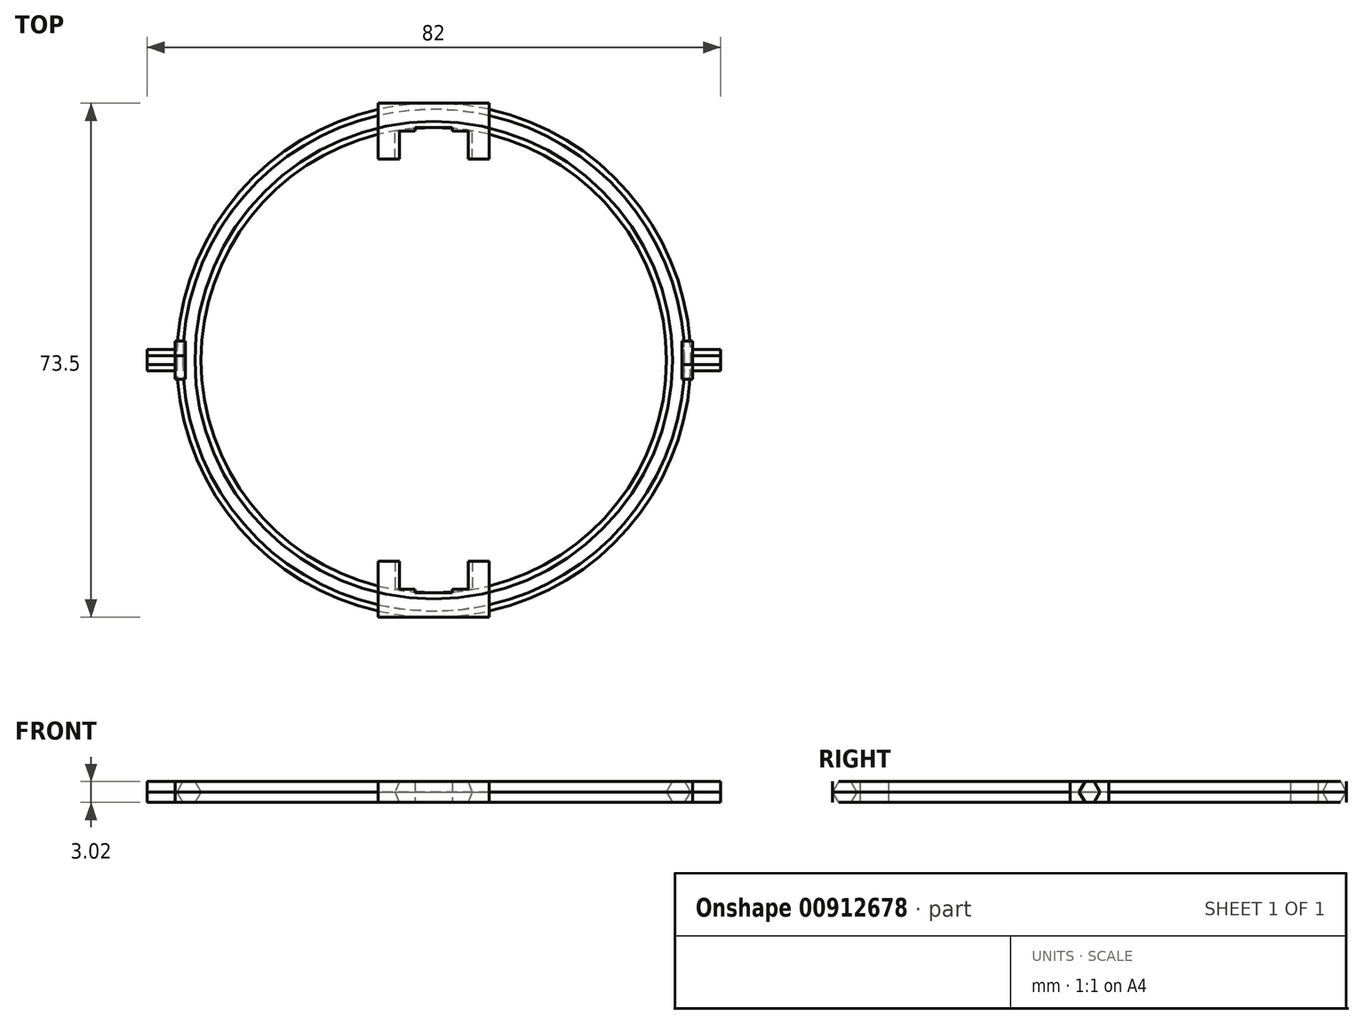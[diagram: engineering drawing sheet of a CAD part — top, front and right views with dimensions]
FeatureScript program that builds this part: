
annotation { "Feature Type Name" : "Feature", "Feature Type Description" : "" }
export const myFeature = defineFeature(function(context is Context, id is Id, definition is map)
    precondition{}
    {
        {
            var Q0;
            Q0=qCreatedBy(makeId("Front.planeOp"),FACE);
            var sketch = newSketch(context, id + "F0", { "sketchPlane" : qUnion([Q0])});
            skCircle(sketch, "E0.cCircle", {"center": v(35, 0) * mm, "radius": 1.73 * mm, "construction": true});
            skLineSegment(sketch, "E0.0", {"start": v(35.86, -1.5) * mm, "end": v(34.12, -1.5) * mm});
            skLineSegment(sketch, "E0.1", {"start": v(34.12, -1.5) * mm, "end": v(33.27, 0.01) * mm});
            skLineSegment(sketch, "E0.2", {"start": v(33.27, 0.01) * mm, "end": v(34.14, 1.5) * mm});
            skLineSegment(sketch, "E0.3", {"start": v(34.14, 1.5) * mm, "end": v(35.88, 1.5) * mm});
            skLineSegment(sketch, "E0.4", {"start": v(35.88, 1.5) * mm, "end": v(36.73, -0.01) * mm});
            skLineSegment(sketch, "E0.5", {"start": v(36.73, -0.01) * mm, "end": v(35.86, -1.5) * mm});
            skLineSegment(sketch, "E1", {"start": v(0, 0) * mm, "end": v(0, 19.8) * mm});
            skSolve(sketch);
        }
        {
            var Q0;
            Q0=makeQuery(id+"F0.imprint","IMPRINT",FACE,{"disambiguationData":[TD([[makeQuery(id+"F0.imprint","IMPRINT",EDGE,{"derivedFrom":sQuery(id+"F0.wireOp",EDGE,"E0.0")}),-1.0]])]});
            var Q1;
            Q1=sQuery(id+"F0.wireOp",EDGE,"E1");
            revolve(context, id + "F1", {"surfaceOperationType" : NewSurfaceOperationType.NEW, "entities" : qUnion([Q0]), "axis" : qUnion([Q1]), "revolveType" : RevolveType.FULL});
        }
        {
            var Q0;
            Q0=qCreatedBy(makeId("Front.planeOp"),FACE);
            var sketch = newSketch(context, id + "F2", { "sketchPlane" : qUnion([Q0])});
            skLineSegment(sketch, "E2", {"start": v(-4.93, 1.5) * mm, "end": v(-5.53, 0) * mm});
            skLineSegment(sketch, "E3", {"start": v(-5.53, 0) * mm, "end": v(-4.93, -1.5) * mm});
            skLineSegment(sketch, "E4", {"start": v(-4.93, -1.5) * mm, "end": v(-7.93, -1.5) * mm});
            skLineSegment(sketch, "E5", {"start": v(-7.93, -1.5) * mm, "end": v(-7.93, 1.5) * mm});
            skLineSegment(sketch, "E6", {"start": v(-7.93, 1.5) * mm, "end": v(-4.93, 1.5) * mm});
            skCircle(sketch, "E7", {"center": v(0, 0) * mm, "radius": 5.15 * mm});
            skCircle(sketch, "E8", {"center": v(0, 0) * mm, "radius": 1.5 * mm});
            skLineSegment(sketch, "E9", {"start": v(0, 1.5) * mm, "end": v(0, -1.5) * mm});
            skLineSegment(sketch, "E10", {"start": v(4.93, 1.5) * mm, "end": v(7.93, 1.5) * mm});
            skLineSegment(sketch, "E11", {"start": v(7.93, 1.5) * mm, "end": v(7.93, -1.5) * mm});
            skLineSegment(sketch, "E12", {"start": v(7.93, -1.5) * mm, "end": v(4.93, -1.5) * mm});
            skLineSegment(sketch, "E13", {"start": v(4.93, -1.5) * mm, "end": v(5.53, 0) * mm});
            skLineSegment(sketch, "E14", {"start": v(5.53, 0) * mm, "end": v(4.93, 1.5) * mm});
            skLineSegment(sketch, "E15", {"start": v(-4.93, 1.5) * mm, "end": v(4.93, 1.5) * mm});
            skLineSegment(sketch, "E16", {"start": v(-4.93, -1.5) * mm, "end": v(4.93, -1.5) * mm});
            skLineSegment(sketch, "E17", {"start": v(-2.68, 1.5) * mm, "end": v(-2.68, -1.5) * mm});
            skLineSegment(sketch, "E18", {"start": v(2.68, 1.5) * mm, "end": v(2.68, -1.5) * mm});
            skSolve(sketch);
        }
        {
            var Q0;
            {var subQ0=sQuery(id+"F2.wireOp",EDGE,"E15");var subQ1=sQuery(id+"F2.wireOp",EDGE,"E8");var subQ2=makeQuery(id+"F2.imprint","INTERSECT",VERTEX,{"disambiguationData":[OD(1.0)],"derivedFrom":[subQ1,subQ0]});Q0=makeQuery(id+"F2.imprint","IMPRINT",FACE,{"disambiguationData":[TD([[makeQuery(id+"F2.imprint","IMPRINT",EDGE,{"disambiguationData":[TD([[subQ2,-1.0]])],"derivedFrom":subQ1}),-1.0]])]});}
            var Q1;
            {var subQ0=sQuery(id+"F2.wireOp",EDGE,"E15");var subQ5=sQuery(id+"F2.wireOp",EDGE,"E17");var subQ6=makeQuery(id+"F2.imprint","INTERSECT",VERTEX,{"derivedFrom":[subQ0,subQ5]});Q1=makeQuery(id+"F2.imprint","IMPRINT",FACE,{"disambiguationData":[TD([[makeQuery(id+"F2.imprint","IMPRINT",EDGE,{"disambiguationData":[TD([[subQ6,-1.0]])],"derivedFrom":subQ5}),-1.0]])]});}
            var Q2;
            {var subQ0=sQuery(id+"F2.wireOp",EDGE,"E15");var subQ1=sQuery(id+"F2.wireOp",EDGE,"E8");var subQ2=makeQuery(id+"F2.imprint","INTERSECT",VERTEX,{"disambiguationData":[OD(1.0)],"derivedFrom":[subQ1,subQ0]});Q2=makeQuery(id+"F2.imprint","IMPRINT",FACE,{"disambiguationData":[TD([[makeQuery(id+"F2.imprint","IMPRINT",EDGE,{"disambiguationData":[TD([[subQ2,-1.0]])],"derivedFrom":subQ1}),1.0]])]});}
            var Q3;
            {var subQ0=sQuery(id+"F2.wireOp",EDGE,"E15");var subQ1=sQuery(id+"F2.wireOp",EDGE,"E8");var subQ2=makeQuery(id+"F2.imprint","INTERSECT",VERTEX,{"disambiguationData":[OD(0.0)],"derivedFrom":[subQ1,subQ0]});Q3=makeQuery(id+"F2.imprint","IMPRINT",FACE,{"disambiguationData":[TD([[makeQuery(id+"F2.imprint","IMPRINT",EDGE,{"disambiguationData":[TD([[subQ2,1.0]])],"derivedFrom":subQ1}),1.0]])]});}
            var Q4;
            Q4=makeQuery(id+"F2.imprint","IMPRINT",FACE,{"disambiguationData":[TD([[makeQuery(id+"F2.imprint","IMPRINT",EDGE,{"derivedFrom":sQuery(id+"F2.wireOp",EDGE,"E2")}),-1.0]])]});
            var Q5;
            {var subQ5=sQuery(id+"F2.wireOp",EDGE,"E18");Q5=makeQuery(id+"F2.imprint","IMPRINT",FACE,{"disambiguationData":[TD([[makeQuery(id+"F2.imprint","IMPRINT",EDGE,{"derivedFrom":subQ5}),-1.0]])]});}
            var Q6;
            {var subQ0=sQuery(id+"F2.wireOp",EDGE,"E2");Q6=makeQuery(id+"F2.imprint","IMPRINT",FACE,{"disambiguationData":[TD([[makeQuery(id+"F2.imprint","IMPRINT",EDGE,{"derivedFrom":subQ0}),1.0]])]});}
            var Q7;
            {var subQ2=sQuery(id+"F2.wireOp",EDGE,"E13");Q7=makeQuery(id+"F2.imprint","IMPRINT",FACE,{"disambiguationData":[TD([[makeQuery(id+"F2.imprint","IMPRINT",EDGE,{"derivedFrom":subQ2}),1.0]])]});}
            var Q8;
            {var subQ5=sQuery(id+"F2.wireOp",EDGE,"E18");Q8=makeQuery(id+"F2.imprint","IMPRINT",FACE,{"disambiguationData":[TD([[makeQuery(id+"F2.imprint","IMPRINT",EDGE,{"derivedFrom":subQ5}),1.0]])]});}
            var Q9;
            Q9=makeQuery(id+"F2.imprint","IMPRINT",FACE,{"disambiguationData":[TD([[makeQuery(id+"F2.imprint","IMPRINT",EDGE,{"derivedFrom":sQuery(id+"F2.wireOp",EDGE,"E10")}),-1.0]])]});
            var Q10;
            {var subQ0=sQuery(id+"F2.wireOp",EDGE,"E9");var subQ1=sQuery(id+"F2.wireOp",EDGE,"E8");var subQ2=makeQuery(id+"F2.imprint","INTERSECT",VERTEX,{"disambiguationData":[OD(0.0)],"derivedFrom":[subQ1,subQ0]});Q10=makeQuery(id+"F2.imprint","IMPRINT",FACE,{"disambiguationData":[TD([[makeQuery(id+"F2.imprint","IMPRINT",EDGE,{"disambiguationData":[TD([[subQ2,-1.0]])],"derivedFrom":subQ1}),1.0]])]});}
            var Q11;
            {var subQ0=sQuery(id+"F2.wireOp",EDGE,"E9");var subQ1=sQuery(id+"F2.wireOp",EDGE,"E8");var subQ2=makeQuery(id+"F2.imprint","INTERSECT",VERTEX,{"disambiguationData":[OD(1.0)],"derivedFrom":[subQ1,subQ0]});Q11=makeQuery(id+"F2.imprint","IMPRINT",FACE,{"disambiguationData":[TD([[makeQuery(id+"F2.imprint","IMPRINT",EDGE,{"disambiguationData":[TD([[subQ2,1.0]])],"derivedFrom":subQ1}),1.0]])]});}
            var Q12;
            {var subQ0=sQuery(id+"F2.wireOp",EDGE,"E9");var subQ1=sQuery(id+"F2.wireOp",EDGE,"E8");var subQ2=makeQuery(id+"F2.imprint","INTERSECT",VERTEX,{"disambiguationData":[OD(1.0)],"derivedFrom":[subQ1,subQ0]});Q12=makeQuery(id+"F2.imprint","IMPRINT",FACE,{"disambiguationData":[TD([[makeQuery(id+"F2.imprint","IMPRINT",EDGE,{"disambiguationData":[TD([[subQ2,-1.0]])],"derivedFrom":subQ1}),1.0]])]});}
            var Q13;
            {var subQ0=sQuery(id+"F2.wireOp",EDGE,"E9");var subQ1=sQuery(id+"F2.wireOp",EDGE,"E8");var subQ2=makeQuery(id+"F2.imprint","INTERSECT",VERTEX,{"disambiguationData":[OD(0.0)],"derivedFrom":[subQ1,subQ0]});Q13=makeQuery(id+"F2.imprint","IMPRINT",FACE,{"disambiguationData":[TD([[makeQuery(id+"F2.imprint","IMPRINT",EDGE,{"disambiguationData":[TD([[subQ2,1.0]])],"derivedFrom":subQ1}),1.0]])]});}
            extrude(context, id + "F3", {"entities" : qUnion([Q0, Q1, Q2, Q3, Q4, Q5, Q6, Q7, Q8, Q9, Q10, Q11, Q12, Q13]), "oppositeDirection" : true, "depth" : 4 * mm, "offsetDistance" : 25 * mm});
        }
        {
            var Q0;
            Q0=makeQuery(id+"F2.imprint","IMPRINT",FACE,{"disambiguationData":[TD([[makeQuery(id+"F2.imprint","IMPRINT",EDGE,{"derivedFrom":sQuery(id+"F2.wireOp",EDGE,"E2")}),-1.0]])]});
            var Q1;
            Q1=makeQuery(id+"F2.imprint","IMPRINT",FACE,{"disambiguationData":[TD([[makeQuery(id+"F2.imprint","IMPRINT",EDGE,{"derivedFrom":sQuery(id+"F2.wireOp",EDGE,"E10")}),-1.0]])]});
            extrude(context, id + "F4", {"entities" : qUnion([Q0, Q1]), "operationType" : NewBodyOperationType.ADD, "depth" : 4 * mm, "offsetDistance" : 25 * mm});
        }
        {
            var Q0;
            {var subQ0=sQuery(id+"F2.wireOp",EDGE,"E15");var subQ1=sQuery(id+"F2.wireOp",EDGE,"E8");var subQ2=makeQuery(id+"F2.imprint","INTERSECT",VERTEX,{"disambiguationData":[OD(1.0)],"derivedFrom":[subQ1,subQ0]});Q0=makeQuery(id+"F2.imprint","IMPRINT",FACE,{"disambiguationData":[TD([[makeQuery(id+"F2.imprint","IMPRINT",EDGE,{"disambiguationData":[TD([[subQ2,-1.0]])],"derivedFrom":subQ1}),1.0]])]});}
            var Q1;
            {var subQ0=sQuery(id+"F2.wireOp",EDGE,"E15");var subQ1=sQuery(id+"F2.wireOp",EDGE,"E8");var subQ2=makeQuery(id+"F2.imprint","INTERSECT",VERTEX,{"disambiguationData":[OD(0.0)],"derivedFrom":[subQ1,subQ0]});Q1=makeQuery(id+"F2.imprint","IMPRINT",FACE,{"disambiguationData":[TD([[makeQuery(id+"F2.imprint","IMPRINT",EDGE,{"disambiguationData":[TD([[subQ2,1.0]])],"derivedFrom":subQ1}),1.0]])]});}
            var Q2;
            {var subQ0=sQuery(id+"F2.wireOp",EDGE,"E15");var subQ1=sQuery(id+"F2.wireOp",EDGE,"E8");var subQ2=makeQuery(id+"F2.imprint","INTERSECT",VERTEX,{"disambiguationData":[OD(1.0)],"derivedFrom":[subQ1,subQ0]});Q2=makeQuery(id+"F2.imprint","IMPRINT",FACE,{"disambiguationData":[TD([[makeQuery(id+"F2.imprint","IMPRINT",EDGE,{"disambiguationData":[TD([[subQ2,-1.0]])],"derivedFrom":subQ1}),-1.0]])]});}
            var Q3;
            {var subQ5=sQuery(id+"F2.wireOp",EDGE,"E18");Q3=makeQuery(id+"F2.imprint","IMPRINT",FACE,{"disambiguationData":[TD([[makeQuery(id+"F2.imprint","IMPRINT",EDGE,{"derivedFrom":subQ5}),-1.0]])]});}
            extrude(context, id + "F5", {"entities" : qUnion([Q0, Q1, Q2, Q3]), "operationType" : NewBodyOperationType.REMOVE, "oppositeDirection" : true, "depth" : 0.5 * mm, "offsetDistance" : 25 * mm});
        }
        {
            var Q0;
            Q0=makeQuery(id+"F3.opExtrude","SWEPT_BODY",BODY,{"disambiguationData":[OSD([sQuery(id+"F2.wireOp",EDGE,"E4"),sQuery(id+"F2.wireOp",EDGE,"E5"),sQuery(id+"F2.wireOp",EDGE,"E6"),sQuery(id+"F2.wireOp",EDGE,"E8"),sQuery(id+"F2.wireOp",EDGE,"E10"),sQuery(id+"F2.wireOp",EDGE,"E11"),sQuery(id+"F2.wireOp",EDGE,"E12"),sQuery(id+"F2.wireOp",EDGE,"E15"),sQuery(id+"F2.wireOp",EDGE,"E16")])]});
            transform(context, id + "F6", {"entities" : qUnion([Q0]), "transformType" : TransformType.TRANSLATION_3D, "dx" : 0 * mm, "dy" : 32.75 * mm, "dz" : 0 * mm, "makeCopy" : false});
        }
        {
            var Q0;
            Q0=qCreatedBy(makeId("Right.planeOp"),FACE);
            var sketch = newSketch(context, id + "F7", { "sketchPlane" : qUnion([Q0])});
            skCircle(sketch, "E19.cCircle", {"center": v(0, 0) * mm, "radius": 1.73 * mm, "construction": true});
            skLineSegment(sketch, "E19.0", {"start": v(0.86, -1.5) * mm, "end": v(-0.88, -1.5) * mm});
            skLineSegment(sketch, "E19.1", {"start": v(-0.88, -1.5) * mm, "end": v(-1.73, 0.01) * mm});
            skLineSegment(sketch, "E19.2", {"start": v(-1.73, 0.01) * mm, "end": v(-0.86, 1.5) * mm});
            skLineSegment(sketch, "E19.3", {"start": v(-0.86, 1.5) * mm, "end": v(0.88, 1.5) * mm});
            skLineSegment(sketch, "E19.4", {"start": v(0.88, 1.5) * mm, "end": v(1.73, -0.01) * mm});
            skLineSegment(sketch, "E19.5", {"start": v(1.73, -0.01) * mm, "end": v(0.86, -1.5) * mm});
            skLineSegment(sketch, "E20.bottom", {"start": v(-2.75, 1.5) * mm, "end": v(2.75, 1.5) * mm});
            skLineSegment(sketch, "E20.top", {"start": v(-2.75, -1.5) * mm, "end": v(2.75, -1.5) * mm});
            skLineSegment(sketch, "E20.left", {"start": v(-2.75, 1.5) * mm, "end": v(-2.75, -1.5) * mm});
            skLineSegment(sketch, "E20.right", {"start": v(2.75, 1.5) * mm, "end": v(2.75, -1.5) * mm});
            skLineSegment(sketch, "E21.0", {"start": v(1.5, -0.01) * mm, "end": v(0.63, -1.5) * mm});
            skLineSegment(sketch, "E21.1", {"start": v(0.65, 1.5) * mm, "end": v(1.5, -0.01) * mm});
            skLineSegment(sketch, "E22.0", {"start": v(-1.5, 0.01) * mm, "end": v(-0.62, 1.5) * mm});
            skLineSegment(sketch, "E22.1", {"start": v(-0.65, -1.5) * mm, "end": v(-1.5, 0.01) * mm});
            skSolve(sketch);
        }
        {
            var Q0;
            {var subQ1=sQuery(id+"F7.wireOp",EDGE,"E21.0");Q0=makeQuery(id+"F7.imprint","IMPRINT",FACE,{"disambiguationData":[TD([[makeQuery(id+"F7.imprint","IMPRINT",EDGE,{"derivedFrom":subQ1}),-1.0]])]});}
            extrude(context, id + "F8", {"entities" : qUnion([Q0]), "depth" : 4 * mm, "offsetDistance" : 25 * mm});
        }
        {
            var Q0;
            {var subQ5=sQuery(id+"F7.wireOp",EDGE,"E19.3");Q0=makeQuery(id+"F7.imprint","IMPRINT",FACE,{"disambiguationData":[TD([[makeQuery(id+"F7.imprint","IMPRINT",EDGE,{"derivedFrom":subQ5}),1.0]])]});}
            var Q1;
            {var subQ1=sQuery(id+"F7.wireOp",EDGE,"E19.1");Q1=makeQuery(id+"F7.imprint","IMPRINT",FACE,{"disambiguationData":[TD([[makeQuery(id+"F7.imprint","IMPRINT",EDGE,{"derivedFrom":subQ1}),1.0]])]});}
            var Q2;
            {var subQ1=sQuery(id+"F7.wireOp",EDGE,"E19.4");Q2=makeQuery(id+"F7.imprint","IMPRINT",FACE,{"disambiguationData":[TD([[makeQuery(id+"F7.imprint","IMPRINT",EDGE,{"derivedFrom":subQ1}),-1.0]])]});}
            var Q3;
            {var subQ1=sQuery(id+"F7.wireOp",EDGE,"E21.0");Q3=makeQuery(id+"F7.imprint","IMPRINT",FACE,{"disambiguationData":[TD([[makeQuery(id+"F7.imprint","IMPRINT",EDGE,{"derivedFrom":subQ1}),-1.0]])]});}
            var Q4;
            {var subQ1=sQuery(id+"F7.wireOp",EDGE,"E19.1");Q4=makeQuery(id+"F7.imprint","IMPRINT",FACE,{"disambiguationData":[TD([[makeQuery(id+"F7.imprint","IMPRINT",EDGE,{"derivedFrom":subQ1}),-1.0]])]});}
            extrude(context, id + "F9", {"entities" : qUnion([Q0, Q1, Q2, Q3, Q4]), "operationType" : NewBodyOperationType.ADD, "oppositeDirection" : true, "depth" : 1.5 * mm, "offsetDistance" : 25 * mm});
        }
        {
            var Q0;
            Q0=makeQuery(id+"F8.opExtrude","SWEPT_BODY",BODY,{"disambiguationData":[OSD([sQuery(id+"F7.wireOp",EDGE,"E19.1"),sQuery(id+"F7.wireOp",EDGE,"E19.2"),sQuery(id+"F7.wireOp",EDGE,"E19.3"),sQuery(id+"F7.wireOp",EDGE,"E19.4"),sQuery(id+"F7.wireOp",EDGE,"E19.5"),sQuery(id+"F7.wireOp",EDGE,"E20.top")])]});
            var Q1;
            Q1=qCreatedBy(makeId("Right.planeOp"),FACE);
            transform(context, id + "F10", {"entities" : qUnion([Q0]), "transformType" : TransformType.TRANSLATION_DISTANCE, "transformDirection" : qUnion([Q1]), "distance" : 37 * mm, "makeCopy" : false});
        }
        {
            var Q0;
            Q0=makeQuery(id+"F8.opExtrude","SWEPT_BODY",BODY,{"disambiguationData":[OSD([sQuery(id+"F7.wireOp",EDGE,"E19.1"),sQuery(id+"F7.wireOp",EDGE,"E19.2"),sQuery(id+"F7.wireOp",EDGE,"E19.3"),sQuery(id+"F7.wireOp",EDGE,"E19.4"),sQuery(id+"F7.wireOp",EDGE,"E19.5"),sQuery(id+"F7.wireOp",EDGE,"E20.top")])]});
            var Q1;
            Q1=makeQuery(id+"F3.opExtrude","SWEPT_BODY",BODY,{"disambiguationData":[OSD([sQuery(id+"F2.wireOp",EDGE,"E4"),sQuery(id+"F2.wireOp",EDGE,"E5"),sQuery(id+"F2.wireOp",EDGE,"E6"),sQuery(id+"F2.wireOp",EDGE,"E10"),sQuery(id+"F2.wireOp",EDGE,"E11"),sQuery(id+"F2.wireOp",EDGE,"E12"),sQuery(id+"F2.wireOp",EDGE,"E15"),sQuery(id+"F2.wireOp",EDGE,"E16")])]});
            var Q2;
            Q2=makeQuery(id+"F1.opRevolve","SWEPT_EDGE",EDGE,{"disambiguationData":[OSD([sQuery(id+"F0.wireOp",EDGE,"E0.4"),sQuery(id+"F0.wireOp",EDGE,"E0.5")])]});
            circularPattern(context, id + "F11", {"entities" : qUnion([Q0, Q1]), "axis" : qUnion([Q2]), "angle" : 360 * degree, "instanceCount" : 2, "equalSpace" : true});
        }
    });
